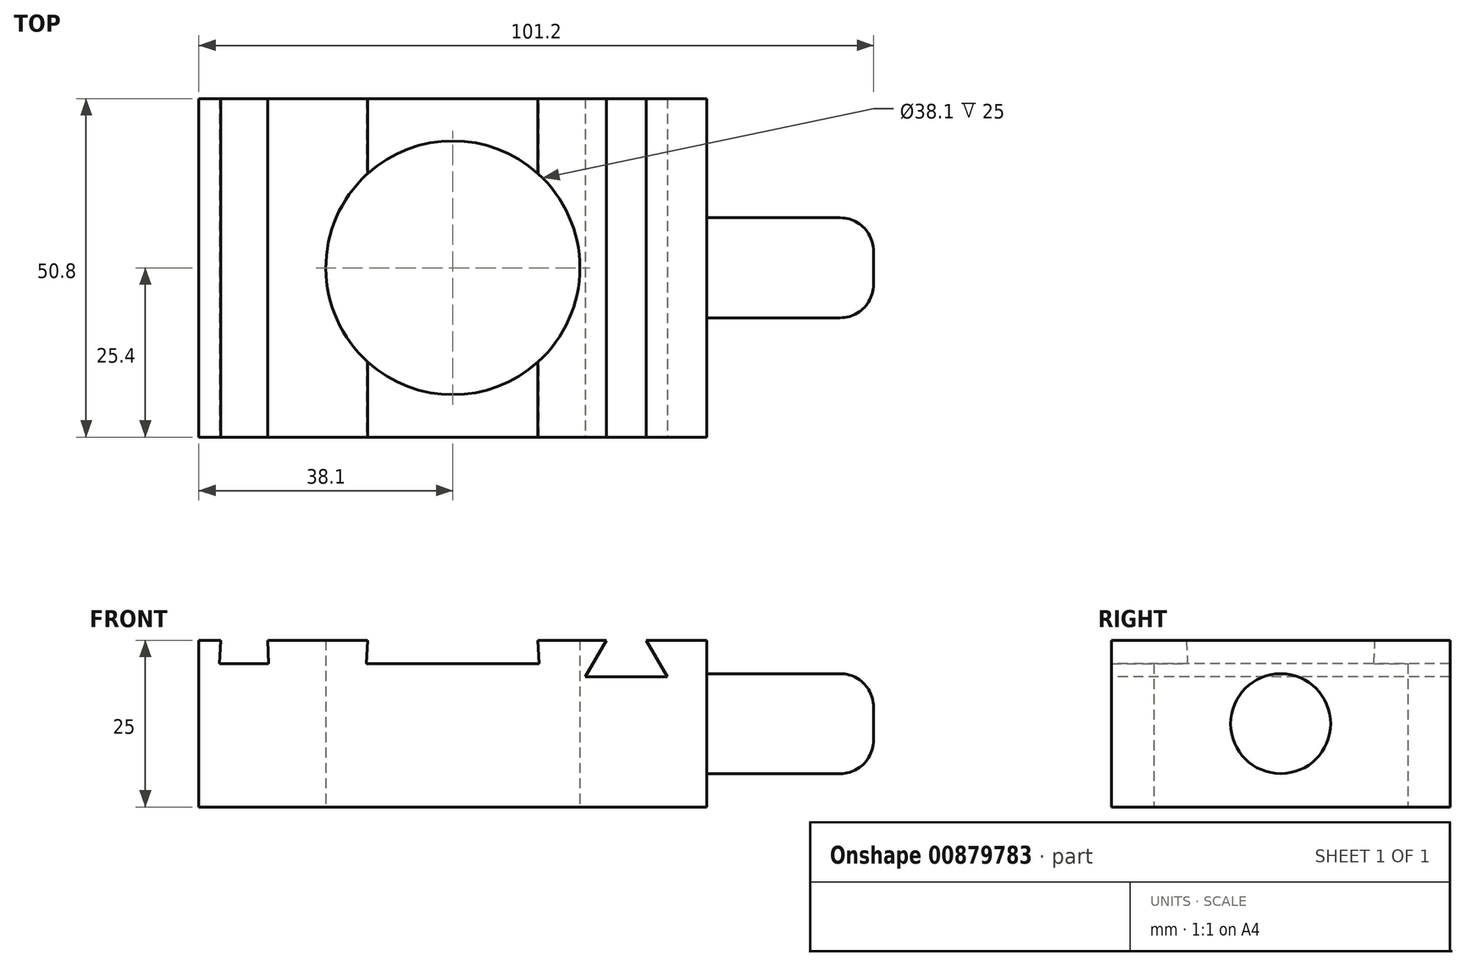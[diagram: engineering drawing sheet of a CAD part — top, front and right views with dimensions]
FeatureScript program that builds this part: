
annotation { "Feature Type Name" : "Feature", "Feature Type Description" : "" }
export const myFeature = defineFeature(function(context is Context, id is Id, definition is map)
    precondition{}
    {
        {
            var Q0;
            Q0=qCreatedBy(makeId("Top.planeOp"),FACE);
            var sketch = newSketch(context, id + "F0", { "sketchPlane" : qUnion([Q0])});
            skLineSegment(sketch, "E0.bottom", {"start": v(-38.1, 25.4) * mm, "end": v(38.1, 25.4) * mm});
            skLineSegment(sketch, "E0.top", {"start": v(-38.1, -25.4) * mm, "end": v(38.1, -25.4) * mm});
            skLineSegment(sketch, "E0.left", {"start": v(-38.1, 25.4) * mm, "end": v(-38.1, -25.4) * mm});
            skLineSegment(sketch, "E0.right", {"start": v(38.1, 25.4) * mm, "end": v(38.1, -25.4) * mm});
            skPoint(sketch, "E0.middle", {"position": v(0, 0) * mm});
            skCircle(sketch, "E1", {"center": v(0, 0) * mm, "radius": 19.05 * mm});
            skSolve(sketch);
        }
        {
            var Q0;
            Q0=makeQuery(id+"F0.imprint","IMPRINT",FACE,{"disambiguationData":[TD([[makeQuery(id+"F0.imprint","IMPRINT",EDGE,{"derivedFrom":sQuery(id+"F0.wireOp",EDGE,"E0.bottom")}),-1.0]])]});
            extrude(context, id + "F1", {"entities" : qUnion([Q0]), "depth" : 25 * mm, "offsetDistance" : 25 * mm});
        }
        {
            var Q0;
            Q0=makeQuery(id+"F1.opExtrude","CAP_FACE",FACE,{"disambiguationData":[OSD([sQuery(id+"F0.wireOp",EDGE,"E0.bottom"),sQuery(id+"F0.wireOp",EDGE,"E0.top"),sQuery(id+"F0.wireOp",EDGE,"E0.left"),sQuery(id+"F0.wireOp",EDGE,"E0.right"),sQuery(id+"F0.wireOp",EDGE,"E1")])],"isStart":false});
            var sketch = newSketch(context, id + "F2", { "sketchPlane" : qUnion([Q0])});
            skLineSegment(sketch, "E2.bottom", {"start": v(-34.8, 25.4) * mm, "end": v(-27.8, 25.4) * mm});
            skLineSegment(sketch, "E2.top", {"start": v(-34.8, -25.4) * mm, "end": v(-27.8, -25.4) * mm});
            skLineSegment(sketch, "E2.left", {"start": v(-34.8, 25.4) * mm, "end": v(-34.8, -25.4) * mm});
            skLineSegment(sketch, "E2.right", {"start": v(-27.8, 25.4) * mm, "end": v(-27.8, -25.4) * mm});
            skLineSegment(sketch, "E3", {"start": v(-12.76, 25.4) * mm, "end": v(-12.76, -25.4) * mm});
            skLineSegment(sketch, "E4", {"start": v(12.76, -25.4) * mm, "end": v(-12.76, -25.4) * mm});
            skLineSegment(sketch, "E5", {"start": v(12.76, -25.4) * mm, "end": v(12.76, 25.4) * mm});
            skLineSegment(sketch, "E6", {"start": v(12.76, 25.4) * mm, "end": v(-12.76, 25.4) * mm});
            skLineSegment(sketch, "E7", {"start": v(0, 25.4) * mm, "end": v(0, -25.4) * mm, "construction": true});
            skSolve(sketch);
        }
        {
            var Q0;
            Q0=makeQuery(id+"F2.imprint","IMPRINT",FACE,{"disambiguationData":[TD([[makeQuery(id+"F2.imprint","IMPRINT",EDGE,{"derivedFrom":sQuery(id+"F2.wireOp",EDGE,"E2.bottom")}),-1.0]])]});
            var Q1;
            {var subQ0=sQuery(id+"F2.wireOp",EDGE,"E4");Q1=makeQuery(id+"F2.imprint","IMPRINT",FACE,{"disambiguationData":[TD([[makeQuery(id+"F2.imprint","IMPRINT",EDGE,{"derivedFrom":subQ0}),1.0]])]});}
            var Q2;
            {var subQ0=sQuery(id+"F2.wireOp",EDGE,"E6");Q2=makeQuery(id+"F2.imprint","IMPRINT",FACE,{"disambiguationData":[TD([[makeQuery(id+"F2.imprint","IMPRINT",EDGE,{"derivedFrom":subQ0}),-1.0]])]});}
            extrude(context, id + "F3", {"entities" : qUnion([Q0, Q1, Q2]), "operationType" : NewBodyOperationType.REMOVE, "oppositeDirection" : true, "depth" : 3.5 * mm, "offsetDistance" : 25 * mm, "hasDraft" : true, "draftAngle" : 3 * degree});
        }
        {
            var Q0;
            Q0=makeQuery(id+"F1.opExtrude","SWEPT_FACE",FACE,{"disambiguationData":[OSD([sQuery(id+"F0.wireOp",EDGE,"E0.top")])]});
            var sketch = newSketch(context, id + "F4", { "sketchPlane" : qUnion([Q0])});
            skLineSegment(sketch, "E8", {"start": v(23, 25) * mm, "end": v(19.82, 19.5) * mm});
            skLineSegment(sketch, "E9", {"start": v(19.82, 19.5) * mm, "end": v(32.18, 19.5) * mm});
            skLineSegment(sketch, "E10", {"start": v(32.18, 19.5) * mm, "end": v(29, 25) * mm});
            skLineSegment(sketch, "E11", {"start": v(29, 25) * mm, "end": v(23, 25) * mm});
            skLineSegment(sketch, "E12", {"start": v(26, 19.5) * mm, "end": v(26, 25) * mm, "construction": true});
            skSolve(sketch);
        }
        {
            var Q0;
            Q0=makeQuery(id+"F4.imprint","IMPRINT",FACE,{"disambiguationData":[TD([[makeQuery(id+"F4.imprint","IMPRINT",EDGE,{"derivedFrom":sQuery(id+"F4.wireOp",EDGE,"E8")}),1.0]])]});
            extrude(context, id + "F5", {"entities" : qUnion([Q0]), "operationType" : NewBodyOperationType.REMOVE, "endBound" : BoundingType.THROUGH_ALL, "oppositeDirection" : true, "depth" : 25 * mm, "offsetDistance" : 25 * mm});
        }
        {
            var Q0;
            Q0=makeQuery(id+"F1.opExtrude","SWEPT_FACE",FACE,{"disambiguationData":[OSD([sQuery(id+"F0.wireOp",EDGE,"E0.right")])]});
            var sketch = newSketch(context, id + "F6", { "sketchPlane" : qUnion([Q0])});
            skCircle(sketch, "E13", {"center": v(0, 12.5) * mm, "radius": 7.5 * mm});
            skPoint(sketch, "E13.centerSnap0", {"position": v(-25.4, 12.5) * mm});
            skPoint(sketch, "E13.centerSnap1", {"position": v(0, 25) * mm});
            skSolve(sketch);
        }
        {
            var Q0;
            Q0=makeQuery(id+"F6.imprint","IMPRINT",FACE,{"disambiguationData":[TD([[makeQuery(id+"F6.imprint","IMPRINT",EDGE,{"derivedFrom":sQuery(id+"F6.wireOp",EDGE,"E13")}),1.0]])]});
            extrude(context, id + "F7", {"entities" : qUnion([Q0]), "operationType" : NewBodyOperationType.ADD, "depth" : 25 * mm, "offsetDistance" : 25 * mm});
        }
        {
            var Q0;
            Q0=makeQuery(id+"F7.opExtrude","CAP_EDGE",EDGE,{"disambiguationData":[OSD([sQuery(id+"F6.wireOp",EDGE,"E13")])],"isStart":false});
            fillet(context, id + "F8", {"entities" : qUnion([Q0]), "radius" : 5 * mm, "tangentPropagation" : true, "allowEdgeOverflow" : false});
        }
    });
